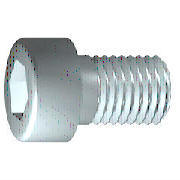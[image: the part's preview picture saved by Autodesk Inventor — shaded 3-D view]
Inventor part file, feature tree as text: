
AUTODESK INVENTOR PART (.ipt)
format: ipt  version: 2017 (Build 210142000, 142)  size: 179,712 bytes
history: native  units: mm (DEFAULTED — no unit token found)
features: sketch x2, extrude x1, plane x1, fillet x1
ambient origin geometry x7: Origin, YZ Plane, XY Plane, X Axis, Y Axis, Z Axis, Center Point
bodies: Solid1 (feature_tree), Body (feature_tree)
feature tree (5):
  extrude  "Slot"  Depth=3.0mm
  plane  "Work Plane1"
  fillet  "Fillet2"  Radius=3.0mm
  sketch  "Sketch1"  dims[d1=18.0mm d2=0.306825mm d3=3.0mm]
  sketch  "Sketch2"  dims[d4=1.5mm d5=60.0deg d6=3.0mm d7=3.0mm d8=2.886751mm d9=5.5mm d10=90.0deg d11=10.0mm d12=0.0mm d13=18.0mm d14=0.0mm d15=0.306725mm d16=0.306725mm d17=0.3mm d19=0.0mm d26=55.0mm d27=45.0deg d28=0.0mm d29=0.0mm d30=0.1mm]
